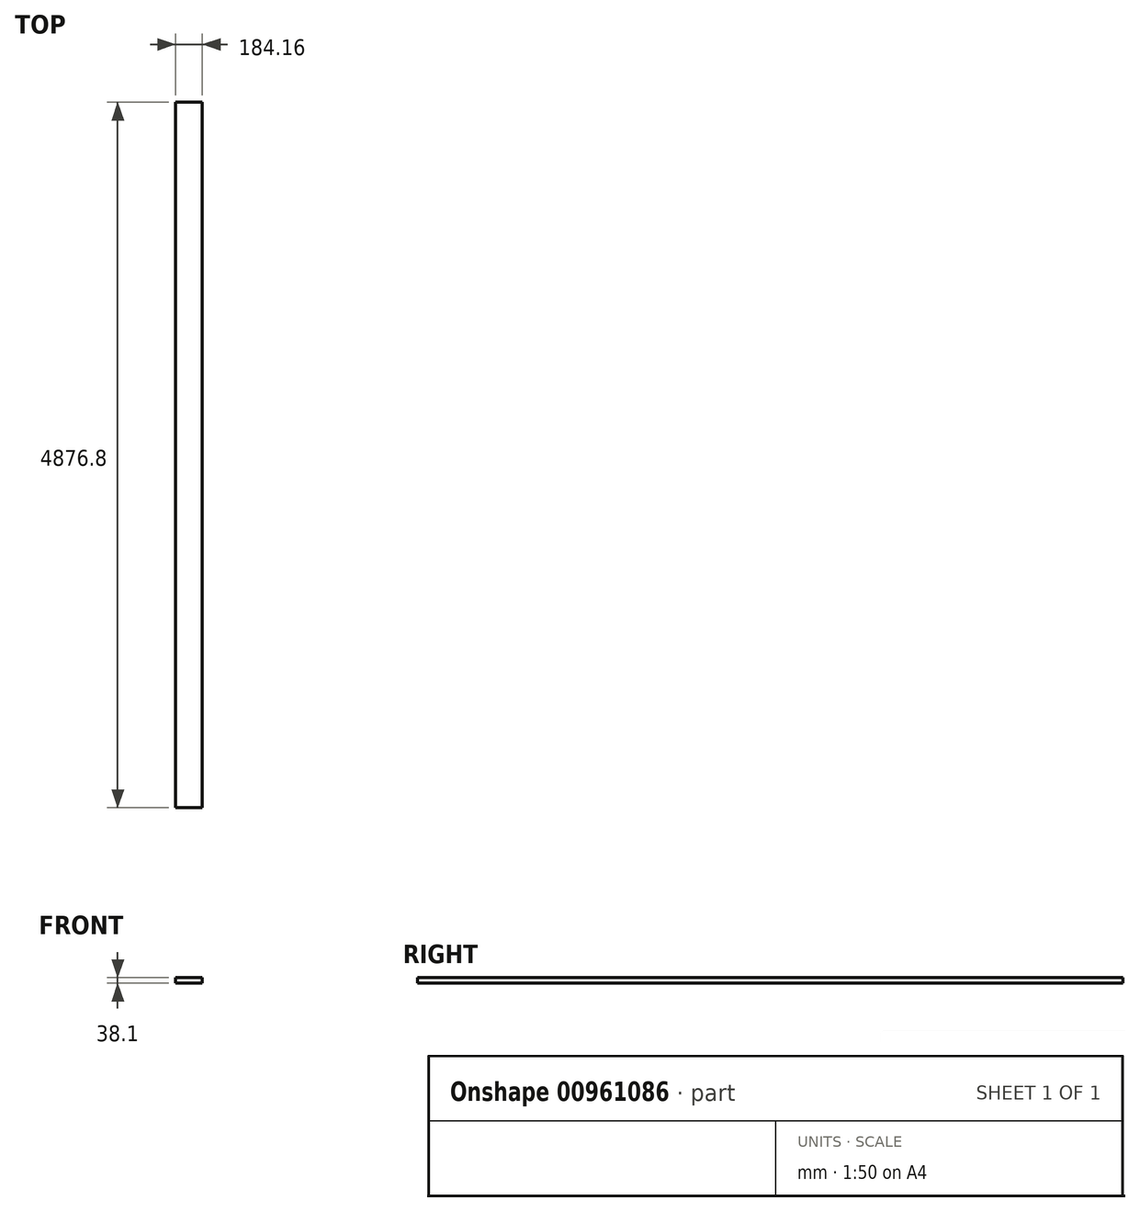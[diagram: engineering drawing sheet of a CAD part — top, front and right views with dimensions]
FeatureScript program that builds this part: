
annotation { "Feature Type Name" : "Feature", "Feature Type Description" : "" }
export const myFeature = defineFeature(function(context is Context, id is Id, definition is map)
    precondition{}
    {
        {
            var Q0;
            Q0=qCreatedBy(makeId("Front.planeOp"),FACE);
            var sketch = newSketch(context, id + "F0", { "sketchPlane" : qUnion([Q0])});
            skLineSegment(sketch, "E0.bottom", {"start": v(92.08, 19.05) * mm, "end": v(-92.08, 19.05) * mm});
            skLineSegment(sketch, "E0.top", {"start": v(92.08, -19.05) * mm, "end": v(-92.08, -19.05) * mm});
            skLineSegment(sketch, "E0.left", {"start": v(92.08, 19.05) * mm, "end": v(92.08, -19.05) * mm});
            skLineSegment(sketch, "E0.right", {"start": v(-92.08, 19.05) * mm, "end": v(-92.08, -19.05) * mm});
            skPoint(sketch, "E0.middle", {"position": v(0, 0) * mm});
            skLineSegment(sketch, "E1.1.0.0", {"start": v(161.92, 19.05) * mm, "end": v(161.92, -19.05) * mm});
            skLineSegment(sketch, "E1.1.0.1", {"start": v(346.08, 19.05) * mm, "end": v(161.92, 19.05) * mm});
            skLineSegment(sketch, "E1.1.0.2", {"start": v(346.08, -19.05) * mm, "end": v(161.92, -19.05) * mm});
            skLineSegment(sketch, "E1.1.0.3", {"start": v(346.08, 19.05) * mm, "end": v(346.08, -19.05) * mm});
            skLineSegment(sketch, "E1.2.0.0", {"start": v(415.93, 19.05) * mm, "end": v(415.93, -19.05) * mm});
            skLineSegment(sketch, "E1.2.0.1", {"start": v(600.08, 19.05) * mm, "end": v(415.93, 19.05) * mm});
            skLineSegment(sketch, "E1.2.0.2", {"start": v(600.08, -19.05) * mm, "end": v(415.93, -19.05) * mm});
            skLineSegment(sketch, "E1.2.0.3", {"start": v(600.08, 19.05) * mm, "end": v(600.08, -19.05) * mm});
            skLineSegment(sketch, "E1.direction1", {"start": v(-92.08, -19.05) * mm, "end": v(161.92, -19.05) * mm, "construction": true});
            skSolve(sketch);
        }
        {
            var Q0;
            Q0=makeQuery(id+"F0.imprint","IMPRINT",FACE,{"disambiguationData":[TD([[makeQuery(id+"F0.imprint","IMPRINT",EDGE,{"derivedFrom":sQuery(id+"F0.wireOp",EDGE,"E0.bottom")}),1.0]])]});
            extrude(context, id + "F1", {"entities" : qUnion([Q0]), "depth" : 4876.8 * mm, "offsetDistance" : 25.4 * mm});
        }
    });
